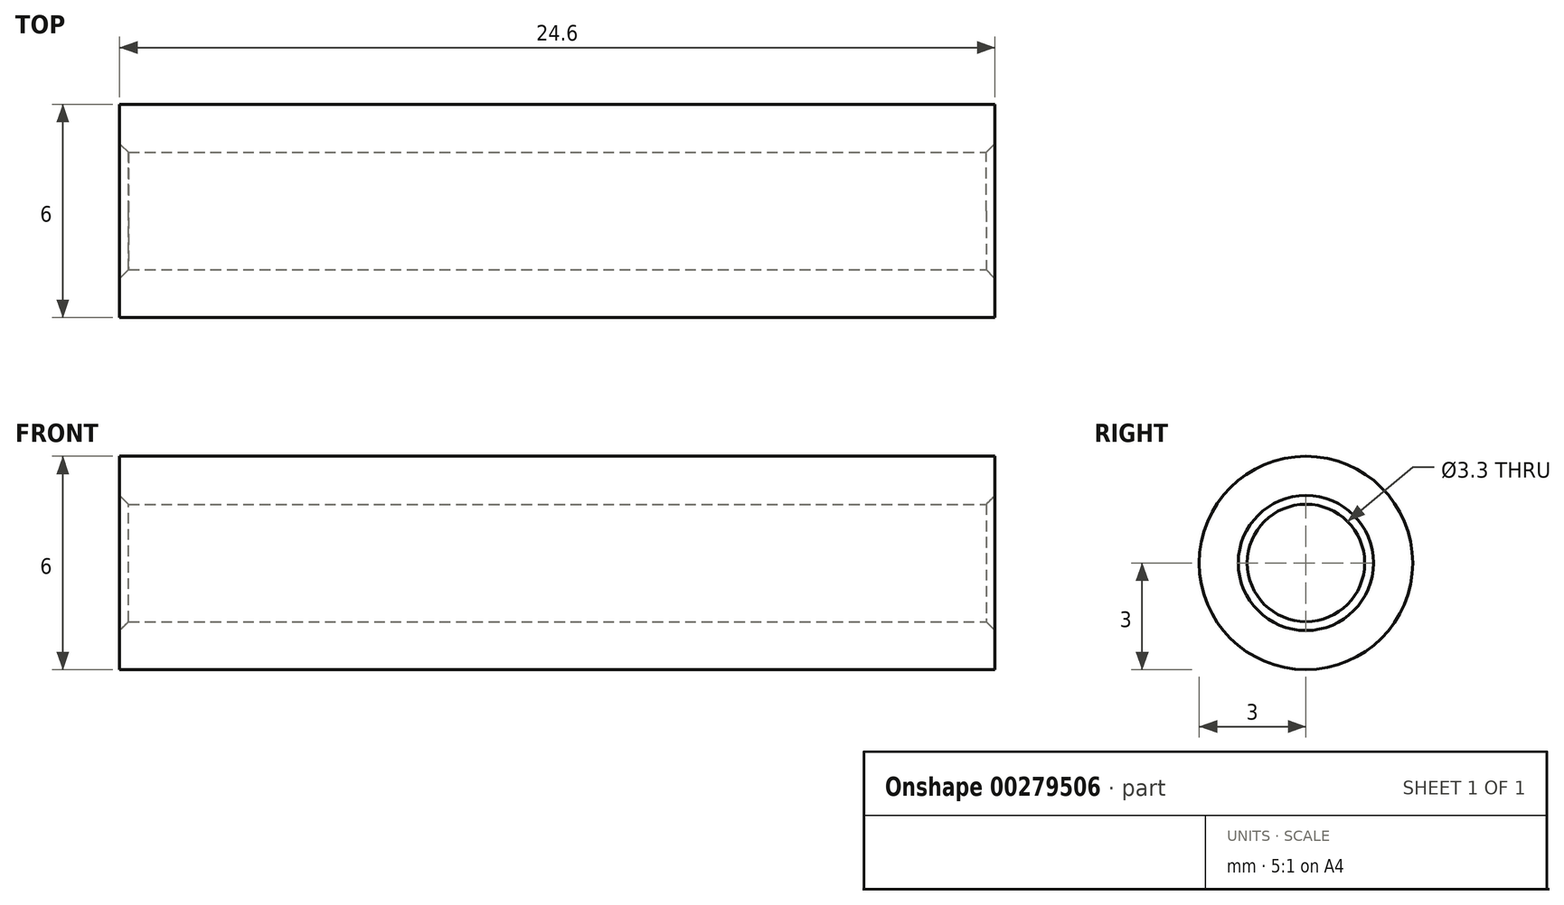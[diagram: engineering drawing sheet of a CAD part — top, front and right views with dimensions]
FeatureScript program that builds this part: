
annotation { "Feature Type Name" : "Feature", "Feature Type Description" : "" }
export const myFeature = defineFeature(function(context is Context, id is Id, definition is map)
    precondition{}
    {
        {
            var Q0;
            Q0=qCreatedBy(makeId("Front.planeOp"),FACE);
            var sketch = newSketch(context, id + "F0", { "sketchPlane" : qUnion([Q0])});
            skLineSegment(sketch, "E0", {"start": v(-12.3, -1.65) * mm, "end": v(-12.3, -3) * mm});
            skLineSegment(sketch, "E1", {"start": v(-12.3, -3) * mm, "end": v(12.3, -3) * mm});
            skLineSegment(sketch, "E2", {"start": v(12.3, -3) * mm, "end": v(12.3, -1.65) * mm});
            skLineSegment(sketch, "E3", {"start": v(12.3, -1.65) * mm, "end": v(-12.3, -1.65) * mm});
            skLineSegment(sketch, "E4", {"start": v(0, 0) * mm, "end": v(-41.12, 0) * mm, "construction": true});
            skSolve(sketch);
        }
        {
            var Q0;
            Q0=makeQuery(id+"F0.imprint","IMPRINT",FACE,{"disambiguationData":[TD([[makeQuery(id+"F0.imprint","IMPRINT",EDGE,{"derivedFrom":sQuery(id+"F0.wireOp",EDGE,"E0")}),1.0]])]});
            var Q1;
            Q1=sQuery(id+"F0.wireOp",EDGE,"E4");
            revolve(context, id + "F1", {"entities" : qUnion([Q0]), "axis" : qUnion([Q1]), "revolveType" : RevolveType.FULL});
        }
        {
            var Q0;
            Q0=makeQuery(id+"F1.opRevolve","SWEPT_FACE",FACE,{"disambiguationData":[OSD([sQuery(id+"F0.wireOp",EDGE,"E3")])]});
            chamfer(context, id + "F2", {"entities" : qUnion([Q0]), "chamferType" : ChamferType.OFFSET_ANGLE, "width" : .25 * mm, "oppositeDirection" : false, "angle" : 45 * degree, "tangentPropagation" : true});
        }
    });
